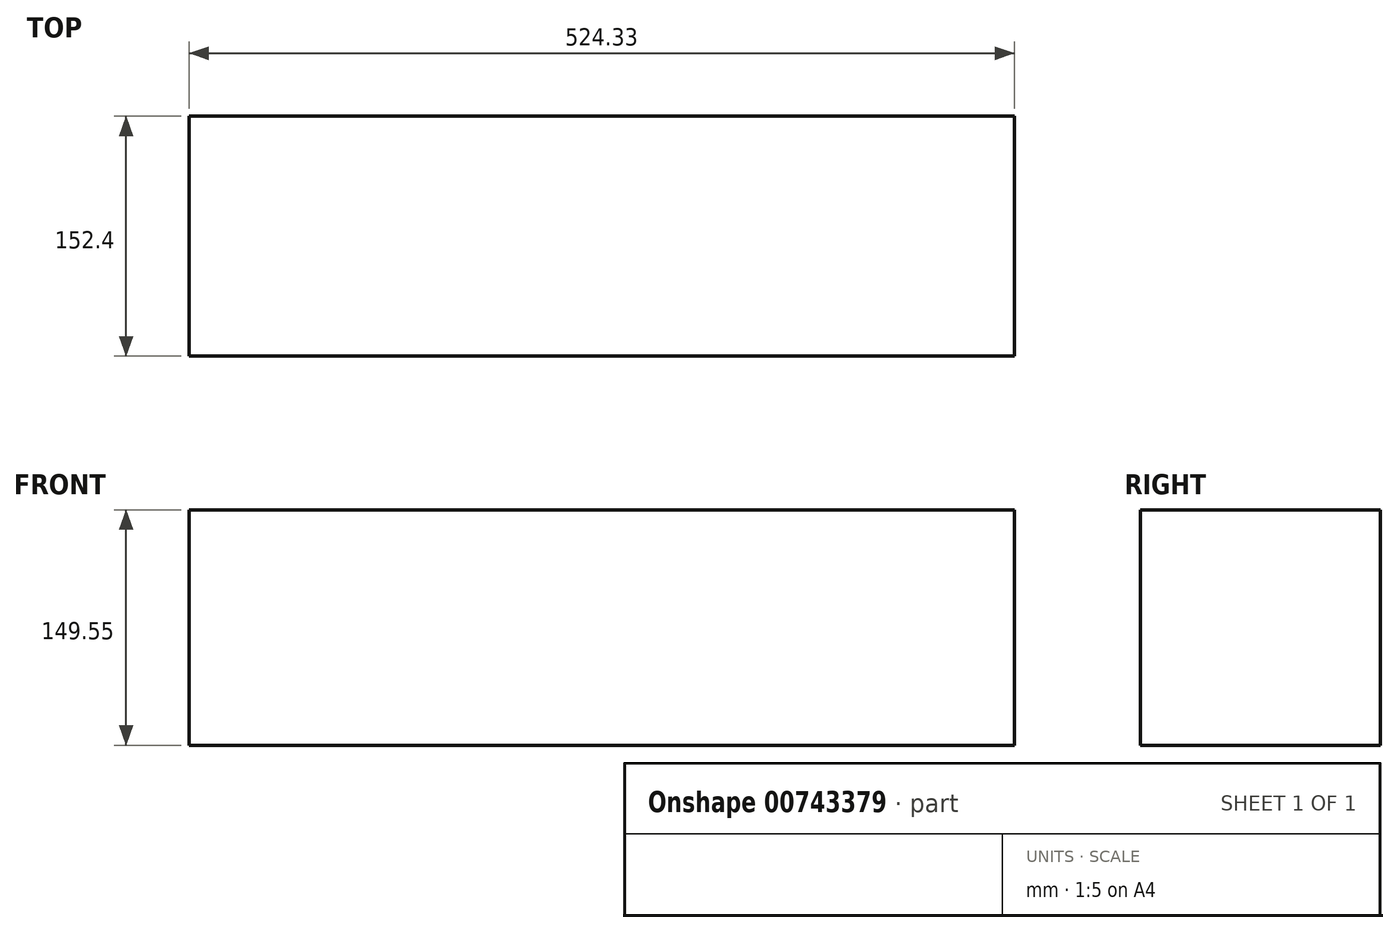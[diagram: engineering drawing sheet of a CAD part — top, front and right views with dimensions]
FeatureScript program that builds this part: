
annotation { "Feature Type Name" : "Feature", "Feature Type Description" : "" }
export const myFeature = defineFeature(function(context is Context, id is Id, definition is map)
    precondition{}
    {
        {
            var Q0;
            Q0=qCreatedBy(makeId("Top.planeOp"),FACE);
            var sketch = newSketch(context, id + "F0", { "sketchPlane" : qUnion([Q0])});
            skLineSegment(sketch, "E0.bottom", {"start": v(0, 152.4) * mm, "end": v(524.33, 152.4) * mm});
            skLineSegment(sketch, "E0.top", {"start": v(0, 0) * mm, "end": v(524.33, 0) * mm});
            skLineSegment(sketch, "E0.left", {"start": v(0, 152.4) * mm, "end": v(0, 0) * mm});
            skLineSegment(sketch, "E0.right", {"start": v(524.33, 152.4) * mm, "end": v(524.33, 0) * mm});
            skSolve(sketch);
        }
        {
            var Q0;
            Q0=makeQuery(id+"F0.imprint","IMPRINT",FACE,{"disambiguationData":[TD([[makeQuery(id+"F0.imprint","IMPRINT",EDGE,{"derivedFrom":sQuery(id+"F0.wireOp",EDGE,"E0.bottom")}),-1.0]])]});
            extrude(context, id + "F1", {"entities" : qUnion([Q0]), "depth" : 149.55 * mm, "offsetDistance" : 25.4 * mm});
        }
    });
